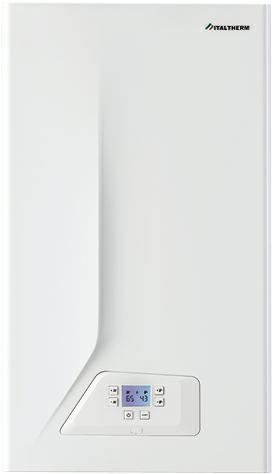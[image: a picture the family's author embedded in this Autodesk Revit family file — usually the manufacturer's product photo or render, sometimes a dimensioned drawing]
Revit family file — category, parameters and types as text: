
# Revit family: City Class K
name_source: partatom
category: Attrezzatura meccanica
units: mm (PartAtom-declared; Revit-internal decimal feet)

## family parameters
Classificazione = Nessuno
Condiviso = No
Host = Muro
Punto di calcolo locali = No
Quota connettore circolare = Usa diametro
Sempre verticale = Sì
Taglio con vuoti quando caricato = No
Tipo di parte = Normale

## types (3) — shared parameters
Combustion air inlet - separate system = 80 mm  [stored 0.262467 ft]
Date of publishing = 22/07/2019
Depth = 324 mm  [stored 1.06299 ft]
Design country = Italy
Domestic Cold Water Diameter = 21 mm  [stored 0.0688976 ft]
Domestic Hot Water Diameter = 21 mm  [stored 0.0688976 ft]
Energetic efficiency (92/42/CEE) = n.d.
Flue outlet = 100 mm  [stored 0.328084 ft]
Gas Inlet Diameter = 26 mm
Height = 700 mm  [stored 2.29659 ft]
Hydronic Return Diameter = 26 mm
Hydronic Supply Diameter = 26 mm
IFC Classification = Boiler
Immagine tipo = city class.jpg
Manufacturer country = Italy
Manufacturer name = Italtherm S.p.A.
Material main = Metal
Material secondary = Plastic
NBS reference Description = Boilers
Omniclass Description = Condensing boilers
Power supply | Frequency (Hz) = 50
Power supply | Phase = 1
Power supply | Voltage (V) = 230 V
Product family = Heating
Product group = Thermal unit
Siphon with condensate drain = 25 mm  [stored 0.082021 ft]
Uniclass 2015 Name = Boilers
Width = 400 mm  [stored 1.31234 ft]
zero-valued in all types: Edition number, Prospetto di default

## per-type parameters (varying)
| type | Efficiency 30% | Maximum heat output 50/30°C | Maximum heat output 80/60°C | Maximum heating heat input | Minimum heat output 50/30°C | Minimum heat output 80/60°C | Nominal efficiency 50/30°C | Nominal efficiency 80/60°C | Power consumption (W) | URL | URL ENG | Weight |
| 25 K | 106.4 | 21.0 | 19.4 | 20 | 2.7 | 2.4 | 105.1 | 96.1 | 73 | www.italtherm.it/g/caldaia-a-gas-da-interno/caldaia-a-condensazione/city-class-k/25-kw | en.italtherm.it/g/wall-hung-condensing-boilers/gas-boiler/city-class-k/25-kw | 28.40 kg |
| 30 K | 106.0 | 25.2 | 23.3 | 24 | 3.1 | 2.8 | 105.2 | 96.0 | 85 | www.italtherm.it/g/caldaia-a-gas-da-interno/caldaia-a-condensazione/city-class-k/30-kw | en.italtherm.it/g/wall-hung-condensing-boilers/gas-boiler/city-class-k/30-kw | 30.20 kg |
| 35 K | 106.7 | 29.5 | 27.4 | 28 | 3.7 | 3.3 | 106.4 | 96.2 | 86 | www.italtherm.it/g/caldaia-a-gas-da-interno/caldaia-a-condensazione/city-class-k/35-kw | en.italtherm.it/g/wall-hung-condensing-boilers/gas-boiler/city-class-k/35-kw | 34.20 kg |

note: [stored X ft] marks values corroborated as IEEE doubles in the binary element streams (Revit-internal decimal feet)
